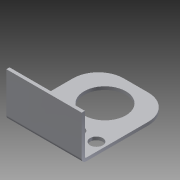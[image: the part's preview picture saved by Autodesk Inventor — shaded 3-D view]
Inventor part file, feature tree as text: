
AUTODESK INVENTOR PART (.ipt)
format: ipt  version: 2013 (Build 170138000, 138)  size: 209,920 bytes
history: native  units: in
note: dims shown in document units (in); Inventor stores cm internally (conversion verified against a paired STEP export)
features: sketch x7, sheet_metal_op x6, other x6, extrude x2, chamfer x1
ambient origin geometry x8: Origin, YZ Plane, XZ Plane, XY Plane, X Axis, Y Axis, Z Axis, Center Point
bodies: Solid1 (feature_tree)
feature tree (22):
  sheet_metal_op  "Face1"
  sheet_metal_op  "Flange1"
  sheet_metal_op  "Face2"
  extrude  "Extrusion1"  Depth=2.0in
  extrude  "Extrusion2"  Depth=1.0in
  chamfer  "Corner Round1"
  sketch  "Sketch1"  dims[d0=1.469in d1=2.0in]
  other  "Plate1"
  sketch  "Sketch2"  dims[d2=1.5in d3=1.0in]
  other  "Plate2"
  sheet_metal_op  "Bend1"
  sheet_metal_op  "Corner1"
  sketch  "Sketch3"  dims[d4=0.125in]
  other  "Plate3"
  sheet_metal_op  "Bend2"
  sketch  "Sketch4"  dims[d5=0.125in]
  sketch  "Sketch5"  dims[d6=0.0625in]
  sketch  "Sketch6"  dims[d7=0.25in]
  sketch  "Sketch8"  dims[d8=0.125in d9=1.5in d10=90.0deg d11=0.05in d12=0.5in d13=0.125in d14=0.125in d15=0.75in d16=0.125in d17=0.125in d18=0.0625in d19=0.25in d20=0.125in d21=0.25in d22=0.0in d23=0.125in d24=0.0in d25=1.222in d26=1.647in d27=0.125in d28=0.0in d29=0.75in d30=0.375in d31=0.5in d32=1.5748in d34=0.75in d35=0.3937in d37=1.0in d39=0.125in d40=0.0in d41=1.0in]
  other  "Cut1"
  other  "Cut2"
  other  "Definition1"
